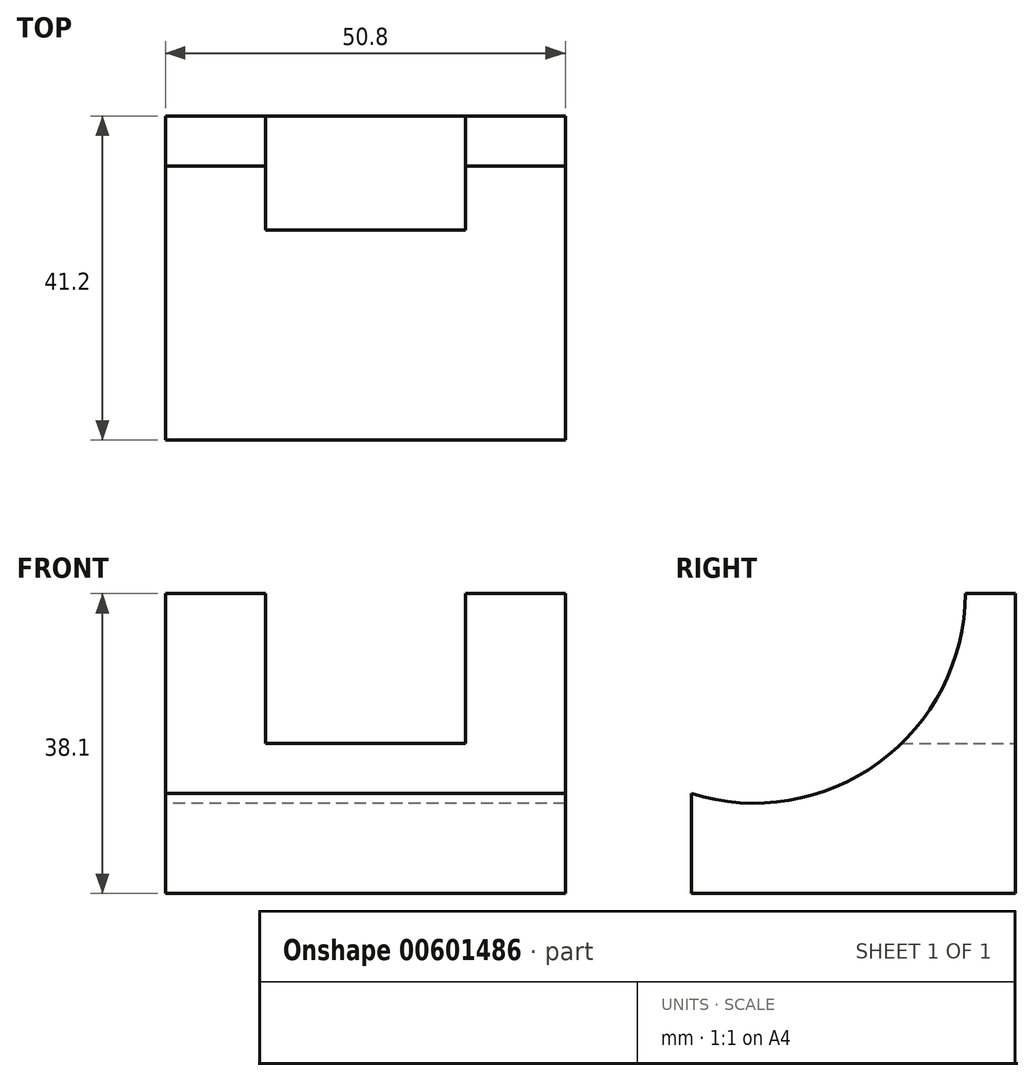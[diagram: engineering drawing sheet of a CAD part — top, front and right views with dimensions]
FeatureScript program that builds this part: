
annotation { "Feature Type Name" : "Feature", "Feature Type Description" : "" }
export const myFeature = defineFeature(function(context is Context, id is Id, definition is map)
    precondition{}
    {
        {
            var Q0;
            Q0=qCreatedBy(makeId("Right.planeOp"),FACE);
            var sketch = newSketch(context, id + "F0", { "sketchPlane" : qUnion([Q0])});
            skLineSegment(sketch, "E0", {"start": v(54.26, 56.56) * mm, "end": v(54.26, 18.46) * mm});
            skLineSegment(sketch, "E1", {"start": v(54.26, 18.46) * mm, "end": v(13.06, 18.46) * mm});
            skLineSegment(sketch, "E2", {"start": v(13.06, 18.46) * mm, "end": v(13.06, 31.16) * mm});
            skLineSegment(sketch, "E3", {"start": v(13.06, 31.16) * mm, "end": v(47.9, 56.56) * mm});
            skLineSegment(sketch, "E4", {"start": v(47.9, 56.56) * mm, "end": v(54.26, 56.56) * mm});
            skSolve(sketch);
        }
        {
            var Q0;
            Q0 = qSketchRegion(id + "F0", true);
            extrude(context, id + "F1", {"entities" : qUnion([Q0]), "depth" : 50.8 * mm, "offsetDistance" : 25.4 * mm});
        }
        {
            var Q0;
            Q0=makeQuery(id+"F1.opExtrude","CAP_FACE",FACE,{"disambiguationData":[OSD([sQuery(id+"F0.wireOp",EDGE,"E0"),sQuery(id+"F0.wireOp",EDGE,"E1"),sQuery(id+"F0.wireOp",EDGE,"E2"),sQuery(id+"F0.wireOp",EDGE,"E3"),sQuery(id+"F0.wireOp",EDGE,"E4")])],"isStart":true});
            var sketch = newSketch(context, id + "F2", { "sketchPlane" : qUnion([Q0])});
            skArc(sketch, "E5", {"start": v(-47.9, 56.56) * mm, "mid": v(-36.87, 35.1) * mm, "end": v(-13.06, 31.16) * mm});
            skLineSegment(sketch, "E6", {"start": v(-47.9, 56.56) * mm, "end": v(-13.06, 31.16) * mm});
            skSolve(sketch);
        }
        {
            var Q0;
            Q0 = qSketchRegion(id + "F2", true);
            extrude(context, id + "F3", {"entities" : qUnion([Q0]), "operationType" : NewBodyOperationType.REMOVE, "oppositeDirection" : true, "depth" : 50.8 * mm, "offsetDistance" : 25.4 * mm});
        }
        {
            var Q0;
            Q0=qCreatedBy(makeId("Front.planeOp"),FACE);
            var sketch = newSketch(context, id + "F4", { "sketchPlane" : qUnion([Q0])});
            skLineSegment(sketch, "E7", {"start": v(12.7, 59.33) * mm, "end": v(12.7, 40.28) * mm});
            skLineSegment(sketch, "E8", {"start": v(12.7, 40.28) * mm, "end": v(38.1, 40.28) * mm});
            skLineSegment(sketch, "E9", {"start": v(38.1, 40.28) * mm, "end": v(38.1, 59.33) * mm});
            skLineSegment(sketch, "E10", {"start": v(12.7, 59.33) * mm, "end": v(38.1, 59.33) * mm});
            skSolve(sketch);
        }
        {
            var Q0;
            Q0 = qSketchRegion(id + "F4", true);
            extrude(context, id + "F5", {"entities" : qUnion([Q0]), "operationType" : NewBodyOperationType.REMOVE, "oppositeDirection" : true, "depth" : 19.05 * mm, "offsetDistance" : 25.4 * mm});
        }
        {
            var Q0;
            Q0=makeQuery(id+"F1.opExtrude","SWEPT_FACE",FACE,{"disambiguationData":[OSD([sQuery(id+"F0.wireOp",EDGE,"E0")])]});
            var sketch = newSketch(context, id + "F6", { "sketchPlane" : qUnion([Q0])});
            skLineSegment(sketch, "E11", {"start": v(-38.1, 56.56) * mm, "end": v(-38.1, 37.51) * mm});
            skLineSegment(sketch, "E12", {"start": v(-38.1, 37.51) * mm, "end": v(-12.7, 37.51) * mm});
            skLineSegment(sketch, "E13", {"start": v(-12.7, 37.51) * mm, "end": v(-12.7, 56.56) * mm});
            skLineSegment(sketch, "E14", {"start": v(-12.7, 56.56) * mm, "end": v(-38.1, 56.56) * mm});
            skSolve(sketch);
        }
        {
            var Q0;
            Q0 = qSketchRegion(id + "F6", true);
            extrude(context, id + "F7", {"entities" : qUnion([Q0]), "operationType" : NewBodyOperationType.REMOVE, "oppositeDirection" : true, "depth" : 19.05 * mm, "offsetDistance" : 25.4 * mm});
        }
    });
